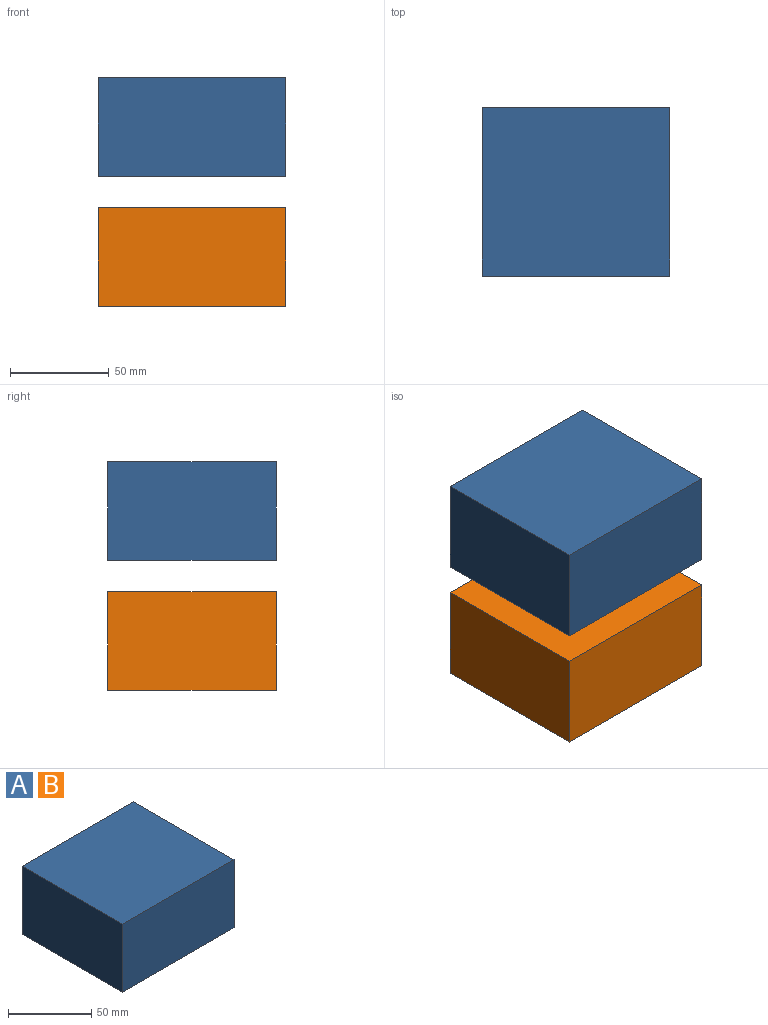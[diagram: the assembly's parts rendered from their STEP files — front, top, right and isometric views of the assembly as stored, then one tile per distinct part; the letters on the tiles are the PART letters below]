
ASSEMBLY  parts=2 mates=1
PART A: 6 faces, bbox 94.6x85.2x50 mm
  f0: plane 94.62x50mm, normal (0,-1,0), area 4730.9mm2, adj f1,f3,f4,f5
  f1: plane 85.21x50mm, normal (1,0,0), area 4260.5mm2, adj f0,f2,f4,f5
  f2: plane 94.62x50mm, normal (0,1,0), area 4730.9mm2, adj f1,f3,f4,f5
  f3: plane 85.21x50mm, normal (-1,0,0), area 4260.5mm2, adj f0,f2,f4,f5
  f4: plane 94.62x85.21mm, normal (0,0,1), area 8062.4mm2, adj f0,f1,f2,f3
  f5: plane 94.62x85.21mm, normal (0,0,-1), area 8062.4mm2, adj f0,f1,f2,f3
PART B: same geometry as A
PLACE A t=(-94.83,2.96,34.08)mm
PLACE B t=(-94.83,2.96,-31.63)mm
MATE slider A.f4 <-> B.f4  axis (0,0,1) through (-94.83,2.96,84.08)mm
